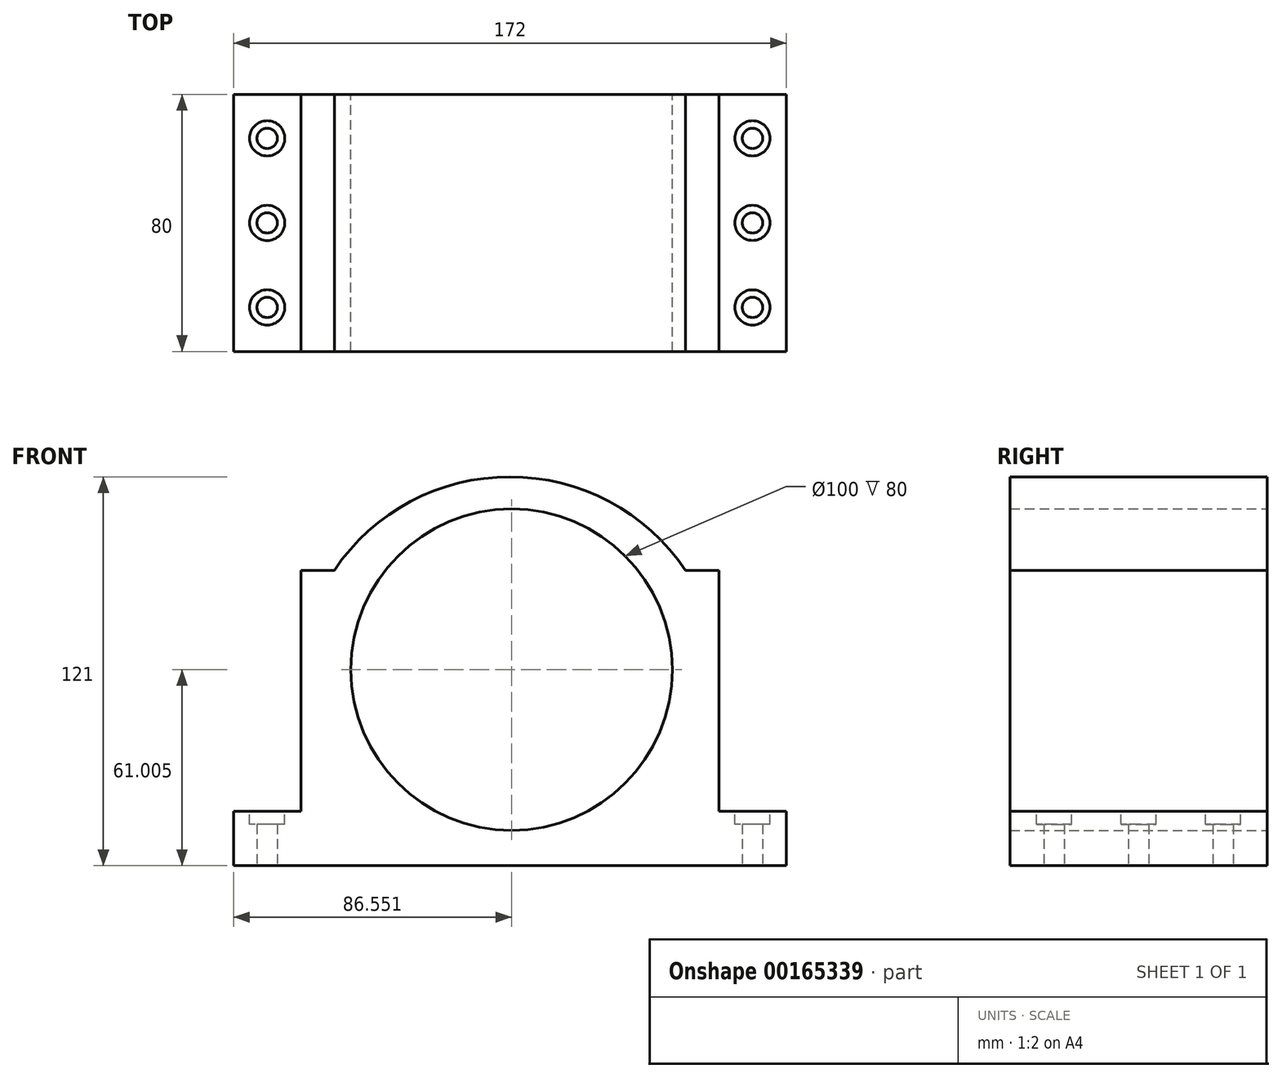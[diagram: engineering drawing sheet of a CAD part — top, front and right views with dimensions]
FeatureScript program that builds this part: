
annotation { "Feature Type Name" : "Feature", "Feature Type Description" : "" }
export const myFeature = defineFeature(function(context is Context, id is Id, definition is map)
    precondition{}
    {
        {
            var Q0;
            Q0=qCreatedBy(makeId("Front.planeOp"),FACE);
            var sketch = newSketch(context, id + "F0", { "sketchPlane" : qUnion([Q0])});
            skLineSegment(sketch, "E0", {"start": v(0, -68.3) * mm, "end": v(86, -68.3) * mm});
            skLineSegment(sketch, "E1", {"start": v(0, -68.3) * mm, "end": v(-86, -68.3) * mm});
            skLineSegment(sketch, "E2", {"start": v(86, -68.3) * mm, "end": v(86, -51.37) * mm});
            skLineSegment(sketch, "E3", {"start": v(-86, -68.3) * mm, "end": v(-86, -51.37) * mm});
            skLineSegment(sketch, "E4", {"start": v(86, -51.37) * mm, "end": v(65, -51.37) * mm});
            skLineSegment(sketch, "E5", {"start": v(-86, -51.37) * mm, "end": v(-65, -51.37) * mm});
            skLineSegment(sketch, "E6", {"start": v(65, -51.37) * mm, "end": v(65, 23.63) * mm});
            skLineSegment(sketch, "E7", {"start": v(-65, -51.37) * mm, "end": v(-65, 23.63) * mm});
            skLineSegment(sketch, "E8", {"start": v(65, 23.63) * mm, "end": v(54.63, 23.63) * mm});
            skLineSegment(sketch, "E9", {"start": v(-65, 23.63) * mm, "end": v(-54.63, 23.63) * mm});
            skArc(sketch, "E10", {"start": v(54.63, 23.63) * mm, "mid": v(0, 52.7) * mm, "end": v(-54.63, 23.63) * mm});
            skLineSegment(sketch, "E11", {"start": v(0, 52.7) * mm, "end": v(0, 42.7) * mm, "construction": true});
            skPoint(sketch, "E11.endSnap0", {"position": v(0, 52.7) * mm});
            skCircle(sketch, "E12", {"center": v(0.55, -7.3) * mm, "radius": 50 * mm});
            skPoint(sketch, "E12.second.point", {"position": v(0, -57.3) * mm});
            skPoint(sketch, "E12.third.point", {"position": v(50.2, -13.16) * mm});
            skSolve(sketch);
        }
        {
            var Q0;
            Q0=qSketchRegion(id+"F0",true);
            extrude(context, id + "F1", {"entities" : qUnion([Q0]), "depth" : 80 * mm});
        }
        {
            var Q0;
            Q0=makeQuery(id+"F1.opExtrude","SWEPT_FACE",FACE,{"disambiguationData":[OSD([sQuery(id+"F0.wireOp",EDGE,"E0"),sQuery(id+"F0.wireOp",EDGE,"E1")])]});
            var sketch = newSketch(context, id + "F2", { "sketchPlane" : qUnion([Q0])});
            skLineSegment(sketch, "E13", {"start": v(-75.5, 80) * mm, "end": v(-75.5, 0) * mm, "construction": true});
            skLineSegment(sketch, "E14", {"start": v(75.5, 80) * mm, "end": v(75.5, 0) * mm, "construction": true});
            skLineSegment(sketch, "E15", {"start": v(86, 13.7) * mm, "end": v(85.76, 12.8) * mm, "construction": true});
            skCircle(sketch, "E16", {"center": v(-75.5, 66.3) * mm, "radius": 3.18 * mm});
            skCircle(sketch, "E17", {"center": v(-75.5, 40) * mm, "radius": 3.18 * mm});
            skCircle(sketch, "E18", {"center": v(-75.5, 13.7) * mm, "radius": 3.18 * mm});
            skCircle(sketch, "E19", {"center": v(75.5, 66.3) * mm, "radius": 3.18 * mm});
            skCircle(sketch, "E20", {"center": v(75.5, 40) * mm, "radius": 3.18 * mm});
            skCircle(sketch, "E21", {"center": v(75.5, 13.7) * mm, "radius": 3.18 * mm});
            skLineSegment(sketch, "E22", {"start": v(-86, 0) * mm, "end": v(86, 0) * mm, "construction": true});
            skLineSegment(sketch, "E23", {"start": v(-86, 80) * mm, "end": v(86, 80) * mm, "construction": true});
            skLineSegment(sketch, "E24", {"start": v(-86, 0) * mm, "end": v(-86, 80) * mm, "construction": true});
            skLineSegment(sketch, "E25", {"start": v(86, 0) * mm, "end": v(86, 80) * mm, "construction": true});
            skLineSegment(sketch, "E26", {"start": v(0, 0) * mm, "end": v(0, 80) * mm, "construction": true});
            skSolve(sketch);
        }
        {
            var Q0;
            Q0=qSketchRegion(id+"F2",true);
            extrude(context, id + "F3", {"entities" : qUnion([Q0]), "operationType" : NewBodyOperationType.REMOVE, "endBound" : BoundingType.THROUGH_ALL, "oppositeDirection" : true, "depth" : 25.4 * mm});
        }
        {
            var Q0;
            Q0=qSketchRegion(id+"F2",true);
            extrude(context, id + "F4", {"entities" : qUnion([Q0]), "operationType" : NewBodyOperationType.REMOVE, "endBound" : BoundingType.THROUGH_ALL, "oppositeDirection" : true, "depth" : 25.4 * mm});
        }
        {
            var Q0;
            Q0=makeQuery(id+"F1.opExtrude","SWEPT_FACE",FACE,{"disambiguationData":[OSD([sQuery(id+"F0.wireOp",EDGE,"E4")])]});
            var sketch = newSketch(context, id + "F5", { "sketchPlane" : qUnion([Q0])});
            skCircle(sketch, "E27", {"center": v(75.5, -13.7) * mm, "radius": 5.48 * mm});
            skCircle(sketch, "E28", {"center": v(75.5, -40) * mm, "radius": 5.48 * mm});
            skCircle(sketch, "E29", {"center": v(75.5, -66.3) * mm, "radius": 5.48 * mm});
            skSolve(sketch);
        }
        {
            var Q0;
            Q0=qSketchRegion(id+"F5",true);
            extrude(context, id + "F6", {"entities" : qUnion([Q0]), "operationType" : NewBodyOperationType.REMOVE, "oppositeDirection" : true, "depth" : 4.06 * mm});
        }
        {
            var Q0;
            Q0=makeQuery(id+"F1.opExtrude","SWEPT_FACE",FACE,{"disambiguationData":[OSD([sQuery(id+"F0.wireOp",EDGE,"E5")])]});
            var sketch = newSketch(context, id + "F7", { "sketchPlane" : qUnion([Q0])});
            skCircle(sketch, "E30", {"center": v(-75.5, -13.7) * mm, "radius": 5.49 * mm});
            skCircle(sketch, "E31", {"center": v(-75.5, -40) * mm, "radius": 5.49 * mm});
            skCircle(sketch, "E32", {"center": v(-75.5, -66.3) * mm, "radius": 5.49 * mm});
            skSolve(sketch);
        }
        {
            var Q0;
            Q0=qSketchRegion(id+"F7",true);
            extrude(context, id + "F8", {"entities" : qUnion([Q0]), "operationType" : NewBodyOperationType.REMOVE, "oppositeDirection" : true, "depth" : 4.06 * mm});
        }
    });
